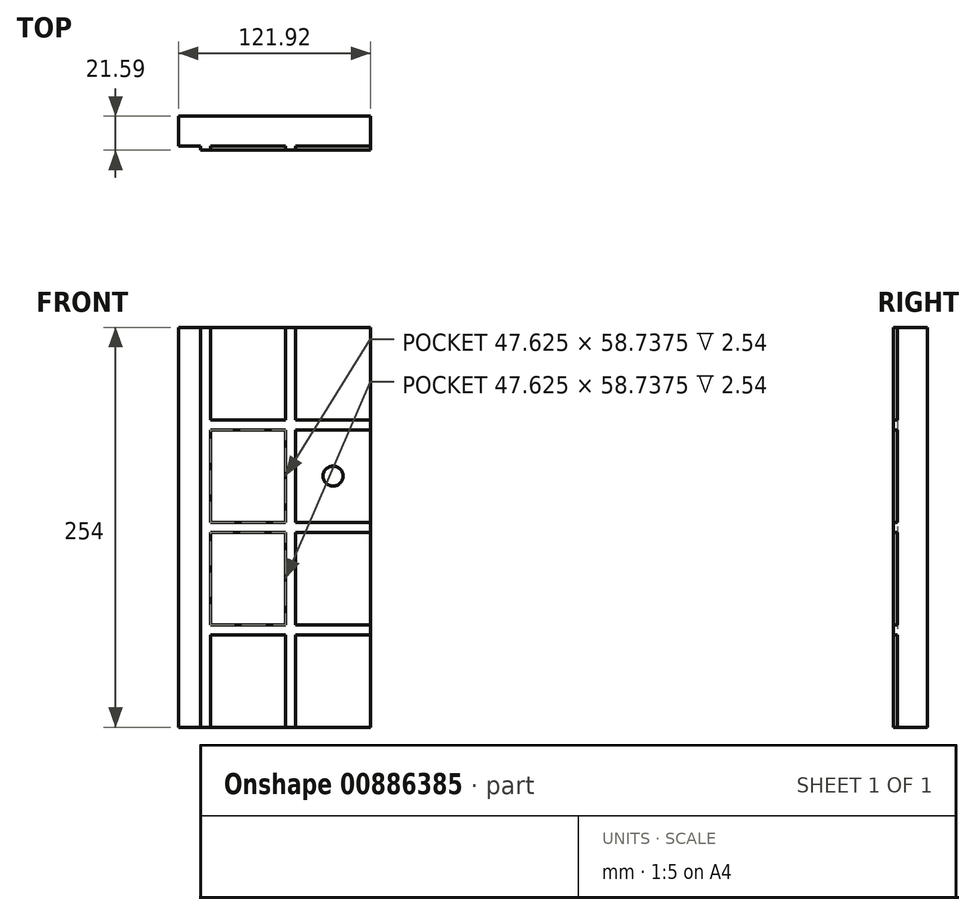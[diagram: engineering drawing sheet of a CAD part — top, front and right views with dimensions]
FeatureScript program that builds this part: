
annotation { "Feature Type Name" : "Feature", "Feature Type Description" : "" }
export const myFeature = defineFeature(function(context is Context, id is Id, definition is map)
    precondition{}
    {
        {
            var Q0;
            Q0=qCreatedBy(makeId("Top.planeOp"),FACE);
            var sketch = newSketch(context, id + "F0", { "sketchPlane" : qUnion([Q0])});
            skLineSegment(sketch, "E0.bottom", {"start": v(-50.8, 9.52) * mm, "end": v(50.8, 9.52) * mm});
            skLineSegment(sketch, "E0.top", {"start": v(-50.8, -9.53) * mm, "end": v(50.8, -9.53) * mm});
            skLineSegment(sketch, "E0.left", {"start": v(-50.8, 9.52) * mm, "end": v(-50.8, -9.53) * mm});
            skLineSegment(sketch, "E0.right", {"start": v(50.8, 9.52) * mm, "end": v(50.8, -9.53) * mm});
            skPoint(sketch, "E0.middle", {"position": v(0, 0) * mm});
            skSolve(sketch);
        }
        {
            var Q0;
            Q0 = qSketchRegion(id + "F0", true);
            extrude(context, id + "F1", {"entities" : qUnion([Q0]), "depth" : 254 * mm, "offsetDistance" : 25.4 * mm});
        }
        {
            var Q0;
            Q0=makeQuery(id+"F1.opExtrude","SWEPT_FACE",FACE,{"disambiguationData":[OSD([sQuery(id+"F0.wireOp",EDGE,"E0.top")])]});
            var sketch = newSketch(context, id + "F2", { "sketchPlane" : qUnion([Q0])});
            skLineSegment(sketch, "E1.bottom", {"start": v(3.17, 254) * mm, "end": v(-3.18, 254) * mm});
            skLineSegment(sketch, "E1.top", {"start": v(3.17, 0) * mm, "end": v(-3.18, 0) * mm});
            skLineSegment(sketch, "E1.left", {"start": v(3.17, 254) * mm, "end": v(3.17, 0) * mm});
            skLineSegment(sketch, "E1.right", {"start": v(-3.18, 254) * mm, "end": v(-3.18, 0) * mm});
            skPoint(sketch, "E1.middle", {"position": v(0, 127) * mm});
            skPoint(sketch, "E1.middle.positionSnap0", {"position": v(50.8, 127) * mm});
            skPoint(sketch, "E1.centerSnap0", {"position": v(50.8, 127) * mm});
            skSolve(sketch);
        }
        {
            var Q0;
            Q0 = qSketchRegion(id + "F2", true);
            extrude(context, id + "F3", {"entities" : qUnion([Q0]), "operationType" : NewBodyOperationType.ADD, "oppositeDirection" : true, "depth" : -2.54 * mm, "offsetDistance" : 25.4 * mm});
        }
        {
            var Q0;
            {var subQ1=sQuery(id+"F0.wireOp",EDGE,"E0.left");var subQ2=sQuery(id+"F0.wireOp",EDGE,"E0.top");Q0=makeQuery(id+"F3.boolean.opBoolean","SPLIT",FACE,{"disambiguationData":[TD([makeQuery(id+"F1.opExtrude","SWEPT_FACE",FACE,{"disambiguationData":[OSD([subQ1])]})])],"derivedFrom":makeQuery(id+"F1.opExtrude","SWEPT_FACE",FACE,{"disambiguationData":[OSD([subQ2])]})});}
            var sketch = newSketch(context, id + "F4", { "sketchPlane" : qUnion([Q0])});
            skLineSegment(sketch, "E2.bottom", {"start": v(-50.8, 130.18) * mm, "end": v(50.8, 130.18) * mm});
            skLineSegment(sketch, "E2.top", {"start": v(-50.8, 123.83) * mm, "end": v(50.8, 123.83) * mm});
            skLineSegment(sketch, "E2.left", {"start": v(-50.8, 130.18) * mm, "end": v(-50.8, 123.83) * mm});
            skLineSegment(sketch, "E2.right", {"start": v(50.8, 130.18) * mm, "end": v(50.8, 123.83) * mm});
            skPoint(sketch, "E2.middle", {"position": v(0, 127) * mm});
            skPoint(sketch, "E2.middle.positionSnap0", {"position": v(-3.18, 127) * mm});
            skPoint(sketch, "E2.centerSnap0", {"position": v(-3.18, 127) * mm});
            skSolve(sketch);
        }
        {
            var Q0;
            {var subQ0=sQuery(id+"F4.wireOp",EDGE,"E2.right");Q0=makeQuery(id+"F4.imprint","IMPRINT",FACE,{"disambiguationData":[TD([[makeQuery(id+"F4.imprint","IMPRINT",EDGE,{"derivedFrom":subQ0}),-1.0]])]});}
            var Q1;
            {var subQ0=sQuery(id+"F4.wireOp",EDGE,"E2.left");Q1=makeQuery(id+"F4.imprint","IMPRINT",FACE,{"disambiguationData":[TD([[makeQuery(id+"F4.imprint","IMPRINT",EDGE,{"derivedFrom":subQ0}),1.0]])]});}
            extrude(context, id + "F5", {"entities" : qUnion([Q0, Q1]), "operationType" : NewBodyOperationType.ADD, "oppositeDirection" : true, "depth" : -2.54 * mm, "offsetDistance" : 25.4 * mm});
        }
        {
            var Q0;
            {var subQ1=sQuery(id+"F0.wireOp",EDGE,"E0.left");var subQ2=sQuery(id+"F0.wireOp",EDGE,"E0.top");var subQ5=makeQuery(id+"F1.opExtrude","SWEPT_FACE",FACE,{"disambiguationData":[OSD([subQ1])]});Q0=makeQuery(id+"F5.boolean.opBoolean","SPLIT",FACE,{"disambiguationData":[TD([makeQuery(id+"F5.opExtrude","SWEPT_FACE",FACE,{"disambiguationData":[OSD([sQuery(id+"F4.wireOp",EDGE,"E2.bottom")])]})])],"derivedFrom":makeQuery(id+"F3.boolean.opBoolean","SPLIT",FACE,{"disambiguationData":[TD([subQ5])],"derivedFrom":makeQuery(id+"F1.opExtrude","SWEPT_FACE",FACE,{"disambiguationData":[OSD([subQ2])]})})});}
            var sketch = newSketch(context, id + "F6", { "sketchPlane" : qUnion([Q0])});
            skLineSegment(sketch, "E3.bottom", {"start": v(-50.8, 195.26) * mm, "end": v(50.8, 195.26) * mm});
            skLineSegment(sketch, "E3.top", {"start": v(-50.8, 188.91) * mm, "end": v(50.8, 188.91) * mm});
            skLineSegment(sketch, "E3.left", {"start": v(-50.8, 195.26) * mm, "end": v(-50.8, 188.91) * mm});
            skLineSegment(sketch, "E3.right", {"start": v(50.8, 195.26) * mm, "end": v(50.8, 188.91) * mm});
            skPoint(sketch, "E3.middle", {"position": v(0, 192.09) * mm});
            skPoint(sketch, "E3.middle.positionSnap0", {"position": v(-50.8, 192.09) * mm});
            skPoint(sketch, "E3.centerSnap0", {"position": v(-50.8, 192.09) * mm});
            skSolve(sketch);
        }
        {
            var Q0;
            Q0 = qSketchRegion(id + "F6", true);
            extrude(context, id + "F7", {"entities" : qUnion([Q0]), "operationType" : NewBodyOperationType.ADD, "oppositeDirection" : true, "depth" : -2.54 * mm, "offsetDistance" : 25.4 * mm});
        }
        {
            var Q0;
            {var subQ1=sQuery(id+"F0.wireOp",EDGE,"E0.left");var subQ2=sQuery(id+"F0.wireOp",EDGE,"E0.top");var subQ6=makeQuery(id+"F1.opExtrude","SWEPT_FACE",FACE,{"disambiguationData":[OSD([subQ1])]});Q0=makeQuery(id+"F5.boolean.opBoolean","SPLIT",FACE,{"disambiguationData":[TD([makeQuery(id+"F5.opExtrude","SWEPT_FACE",FACE,{"disambiguationData":[OSD([sQuery(id+"F4.wireOp",EDGE,"E2.top")])]})])],"derivedFrom":makeQuery(id+"F3.boolean.opBoolean","SPLIT",FACE,{"disambiguationData":[TD([subQ6])],"derivedFrom":makeQuery(id+"F1.opExtrude","SWEPT_FACE",FACE,{"disambiguationData":[OSD([subQ2])]})})});}
            var sketch = newSketch(context, id + "F8", { "sketchPlane" : qUnion([Q0])});
            skLineSegment(sketch, "E4.bottom", {"start": v(-50.8, 65.09) * mm, "end": v(50.8, 65.09) * mm});
            skLineSegment(sketch, "E4.top", {"start": v(-50.8, 58.74) * mm, "end": v(50.8, 58.74) * mm});
            skLineSegment(sketch, "E4.left", {"start": v(-50.8, 65.09) * mm, "end": v(-50.8, 58.74) * mm});
            skLineSegment(sketch, "E4.right", {"start": v(50.8, 65.09) * mm, "end": v(50.8, 58.74) * mm});
            skPoint(sketch, "E4.middle", {"position": v(0, 61.91) * mm});
            skPoint(sketch, "E4.middle.positionSnap0", {"position": v(-3.18, 61.91) * mm});
            skPoint(sketch, "E4.centerSnap0", {"position": v(-3.18, 61.91) * mm});
            skSolve(sketch);
        }
        {
            var Q0;
            Q0 = qSketchRegion(id + "F8", true);
            extrude(context, id + "F9", {"entities" : qUnion([Q0]), "operationType" : NewBodyOperationType.ADD, "oppositeDirection" : true, "depth" : -2.54 * mm, "offsetDistance" : 25.4 * mm});
        }
        {
            var Q0;
            {var subQ1=sQuery(id+"F0.wireOp",EDGE,"E0.right");var subQ2=makeQuery(id+"F1.opExtrude","SWEPT_FACE",FACE,{"disambiguationData":[OSD([subQ1])]});var subQ4=makeQuery(id+"F5.opExtrude","SWEPT_FACE",FACE,{"disambiguationData":[OSD([sQuery(id+"F4.wireOp",EDGE,"E2.bottom")])]});var subQ5=makeQuery(id+"F3.opExtrude","SWEPT_FACE",FACE,{"disambiguationData":[OSD([sQuery(id+"F2.wireOp",EDGE,"E1.bottom")])]});var subQ7=sQuery(id+"F0.wireOp",EDGE,"E0.top");Q0=makeQuery(id+"F7.boolean.opBoolean","SPLIT",FACE,{"disambiguationData":[TD([subQ4])],"derivedFrom":makeQuery(id+"F5.boolean.opBoolean","SPLIT",FACE,{"disambiguationData":[TD([subQ5])],"derivedFrom":makeQuery(id+"F3.boolean.opBoolean","SPLIT",FACE,{"disambiguationData":[TD([subQ2])],"derivedFrom":makeQuery(id+"F1.opExtrude","SWEPT_FACE",FACE,{"disambiguationData":[OSD([subQ7])]})})})});}
            var sketch = newSketch(context, id + "F10", { "sketchPlane" : qUnion([Q0])});
            skCircle(sketch, "E5", {"center": v(26.99, 159.54) * mm, "radius": 6.35 * mm});
            skPoint(sketch, "E5.centerSnap0", {"position": v(50.8, 159.54) * mm});
            skPoint(sketch, "E5.centerSnap1", {"position": v(26.99, 130.18) * mm});
            skSolve(sketch);
        }
        {
            var Q0;
            Q0 = qSketchRegion(id + "F10", true);
            extrude(context, id + "F11", {"entities" : qUnion([Q0]), "operationType" : NewBodyOperationType.ADD, "depth" : 0.25 * mm, "offsetDistance" : 25.4 * mm});
        }
        {
            var Q0;
            Q0=makeQuery(id+"F9.boolean.opBoolean","MERGE",FACE,{"derivedFrom":[makeQuery(id+"F7.boolean.opBoolean","MERGE",FACE,{"derivedFrom":[makeQuery(id+"F5.boolean.opBoolean","MERGE",FACE,{"derivedFrom":[makeQuery(id+"F1.opExtrude","SWEPT_FACE",FACE,{"disambiguationData":[OSD([sQuery(id+"F0.wireOp",EDGE,"E0.left")])]}),makeQuery(id+"F5.opExtrude","SWEPT_FACE",FACE,{"disambiguationData":[OSD([sQuery(id+"F4.wireOp",EDGE,"E2.left")])]})]}),makeQuery(id+"F7.opExtrude","SWEPT_FACE",FACE,{"disambiguationData":[OSD([sQuery(id+"F6.wireOp",EDGE,"E3.left")])]})]}),makeQuery(id+"F9.opExtrude","SWEPT_FACE",FACE,{"disambiguationData":[OSD([sQuery(id+"F8.wireOp",EDGE,"E4.left")])]})]});
            var sketch = newSketch(context, id + "F12", { "sketchPlane" : qUnion([Q0])});
            skLineSegment(sketch, "E6.bottom", {"start": v(-9.52, 254) * mm, "end": v(9.52, 254) * mm});
            skLineSegment(sketch, "E6.top", {"start": v(-9.52, 0) * mm, "end": v(9.52, 0) * mm});
            skLineSegment(sketch, "E6.left", {"start": v(-9.52, 254) * mm, "end": v(-9.52, 0) * mm});
            skLineSegment(sketch, "E6.right", {"start": v(9.52, 254) * mm, "end": v(9.52, 0) * mm});
            skPoint(sketch, "E6.middle", {"position": v(0, 127) * mm});
            skPoint(sketch, "E6.middle.positionSnap0", {"position": v(12.07, 127) * mm});
            skPoint(sketch, "E6.centerSnap0", {"position": v(12.07, 127) * mm});
            skSolve(sketch);
        }
        {
            var Q0;
            Q0 = qSketchRegion(id + "F12", true);
            extrude(context, id + "F13", {"entities" : qUnion([Q0]), "operationType" : NewBodyOperationType.ADD, "depth" : 20.32 * mm, "offsetDistance" : 25.4 * mm});
        }
        {
            var Q0;
            {var subQ1=makeQuery(id+"F5.opExtrude","SWEPT_FACE",FACE,{"disambiguationData":[OSD([sQuery(id+"F4.wireOp",EDGE,"E2.top")])]});var subQ4=sQuery(id+"F0.wireOp",EDGE,"E0.left");var subQ5=makeQuery(id+"F1.opExtrude","SWEPT_FACE",FACE,{"disambiguationData":[OSD([subQ4])]});var subQ7=makeQuery(id+"F3.opExtrude","SWEPT_FACE",FACE,{"disambiguationData":[OSD([sQuery(id+"F2.wireOp",EDGE,"E1.top")])]});var subQ9=sQuery(id+"F0.wireOp",EDGE,"E0.top");var subQ12=makeQuery(id+"F3.opExtrude","SWEPT_FACE",FACE,{"disambiguationData":[OSD([sQuery(id+"F2.wireOp",EDGE,"E1.bottom")])]});var subQ14=makeQuery(id+"F3.boolean.opBoolean","SPLIT",FACE,{"disambiguationData":[TD([subQ5])],"derivedFrom":makeQuery(id+"F1.opExtrude","SWEPT_FACE",FACE,{"disambiguationData":[OSD([subQ9])]})});var subQ15=makeQuery(id+"F5.boolean.opBoolean","SPLIT",FACE,{"disambiguationData":[TD([subQ7])],"derivedFrom":subQ14});var subQ16=makeQuery(id+"F5.opExtrude","SWEPT_FACE",FACE,{"disambiguationData":[OSD([sQuery(id+"F4.wireOp",EDGE,"E2.bottom")])]});var subQ17=makeQuery(id+"F5.boolean.opBoolean","SPLIT",FACE,{"disambiguationData":[TD([subQ12])],"derivedFrom":subQ14});Q0=makeQuery(id+"F13.boolean.opBoolean","MERGE",FACE,{"derivedFrom":[makeQuery(id+"F7.boolean.opBoolean","SPLIT",FACE,{"disambiguationData":[TD([subQ12])],"derivedFrom":subQ17}),makeQuery(id+"F7.boolean.opBoolean","SPLIT",FACE,{"disambiguationData":[TD([subQ16])],"derivedFrom":subQ17}),makeQuery(id+"F9.boolean.opBoolean","SPLIT",FACE,{"disambiguationData":[TD([subQ7])],"derivedFrom":subQ15}),makeQuery(id+"F9.boolean.opBoolean","SPLIT",FACE,{"disambiguationData":[TD([subQ1])],"derivedFrom":subQ15}),makeQuery(id+"F13.opExtrude","SWEPT_FACE",FACE,{"disambiguationData":[OSD([sQuery(id+"F12.wireOp",EDGE,"E6.right")])]})]});}
            var sketch = newSketch(context, id + "F14", { "sketchPlane" : qUnion([Q0])});
            skLineSegment(sketch, "E7", {"start": v(-50.8, 127) * mm, "end": v(-50.8, 254) * mm});
            skLineSegment(sketch, "E8", {"start": v(-50.8, 254) * mm, "end": v(-57.15, 254) * mm});
            skLineSegment(sketch, "E9", {"start": v(-57.15, 254) * mm, "end": v(-57.15, 0) * mm});
            skLineSegment(sketch, "E10", {"start": v(-57.15, 0) * mm, "end": v(-50.8, 0) * mm});
            skLineSegment(sketch, "E11", {"start": v(-50.8, 0) * mm, "end": v(-50.8, 123.83) * mm});
            skLineSegment(sketch, "E12", {"start": v(-50.8, 123.83) * mm, "end": v(-50.8, 128.69) * mm});
            skSolve(sketch);
        }
        {
            var Q0;
            Q0 = qSketchRegion(id + "F14", true);
            extrude(context, id + "F15", {"entities" : qUnion([Q0]), "operationType" : NewBodyOperationType.ADD, "depth" : 2.54 * mm, "offsetDistance" : 25.4 * mm});
        }
    });
